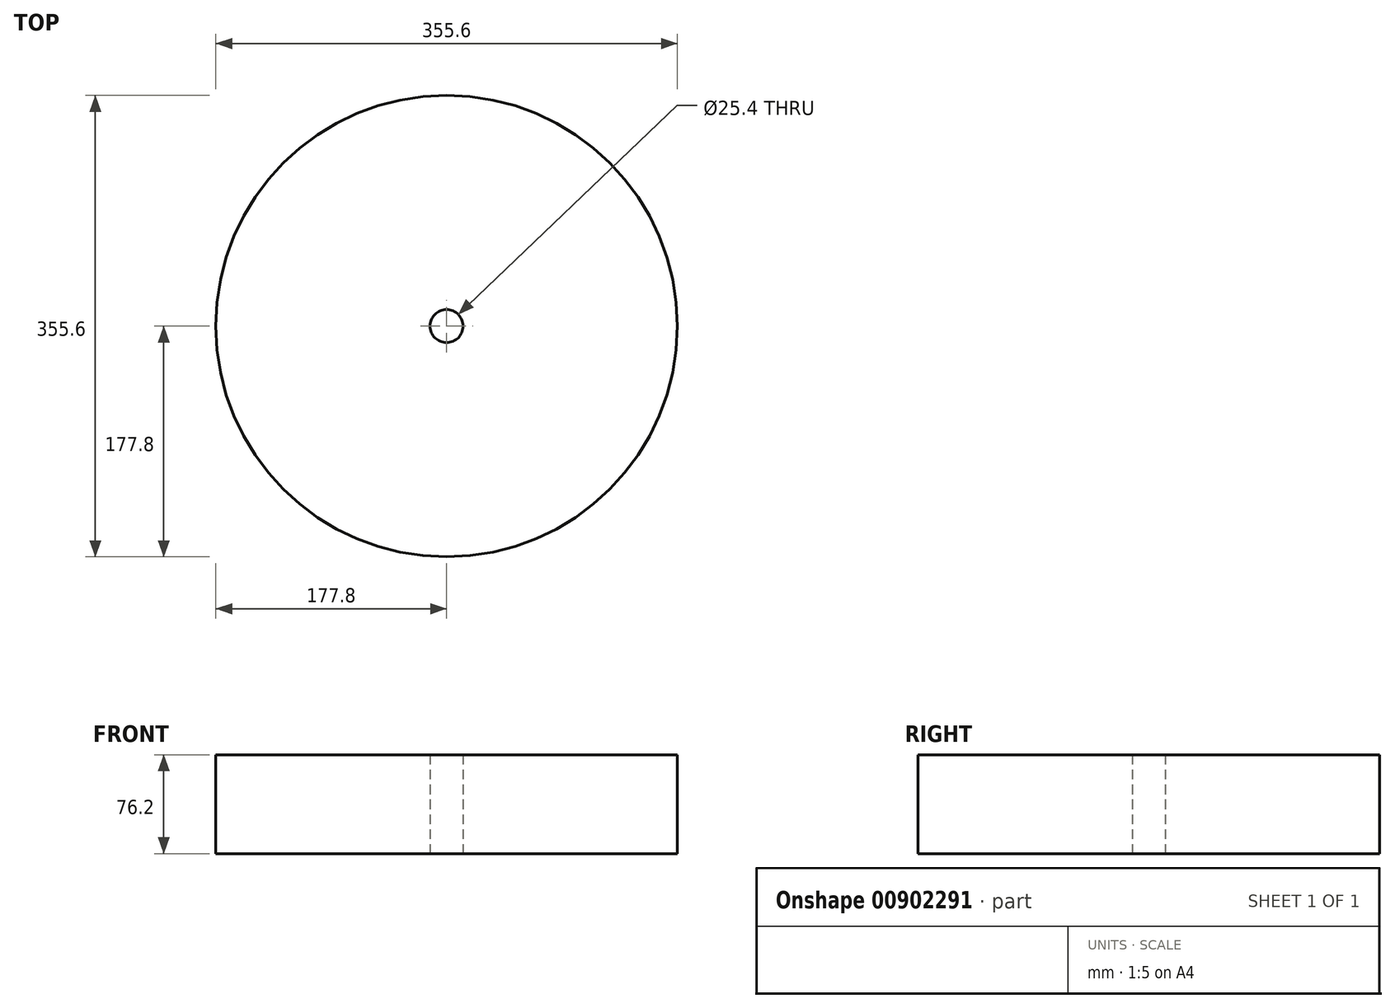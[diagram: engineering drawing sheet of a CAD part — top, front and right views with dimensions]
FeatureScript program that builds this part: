
annotation { "Feature Type Name" : "Feature", "Feature Type Description" : "" }
export const myFeature = defineFeature(function(context is Context, id is Id, definition is map)
    precondition{}
    {
        {
            var Q0;
            Q0=qCreatedBy(makeId("Top.planeOp"),FACE);
            var sketch = newSketch(context, id + "F0", { "sketchPlane" : qUnion([Q0])});
            skCircle(sketch, "E0", {"center": v(0, 0) * mm, "radius": 177.8 * mm});
            skCircle(sketch, "E1", {"center": v(0, 0) * mm, "radius": 12.7 * mm});
            skSolve(sketch);
        }
        {
            var Q0;
            Q0 = qSketchRegion(id + "F0", true);
            extrude(context, id + "F1", {"entities" : qUnion([Q0]), "depth" : 76.2 * mm, "offsetDistance" : 25.4 * mm});
        }
    });
